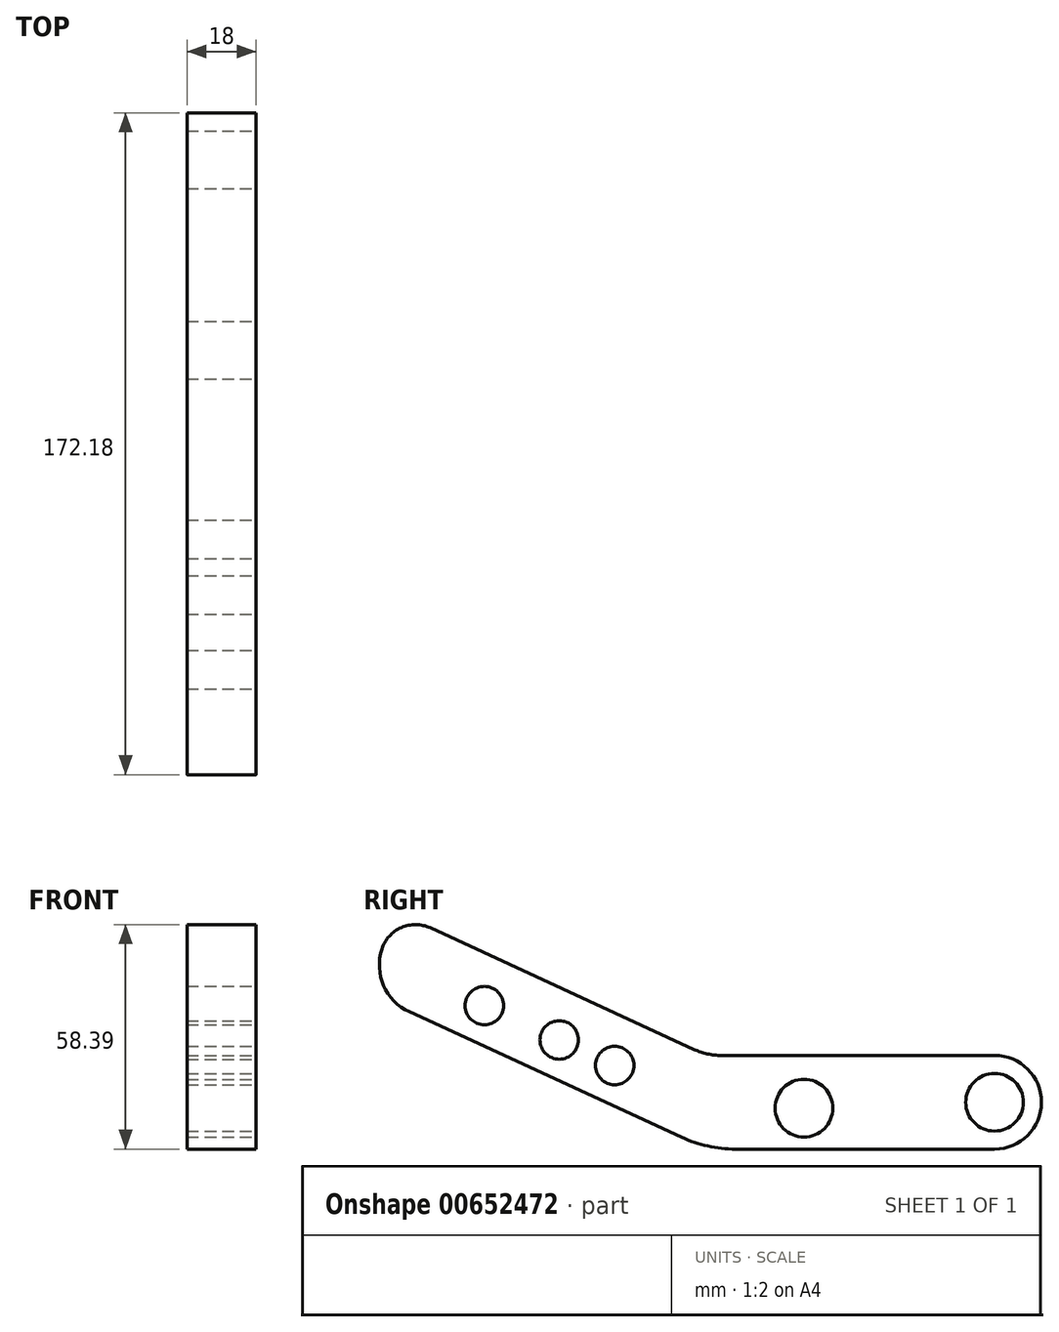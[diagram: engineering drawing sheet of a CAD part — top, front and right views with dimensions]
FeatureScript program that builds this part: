
annotation { "Feature Type Name" : "Feature", "Feature Type Description" : "" }
export const myFeature = defineFeature(function(context is Context, id is Id, definition is map)
    precondition{}
    {
        {
            var Q0;
            Q0=qCreatedBy(makeId("Right.planeOp"),FACE);
            var sketch = newSketch(context, id + "F0", { "sketchPlane" : qUnion([Q0])});
            skLineSegment(sketch, "E0", {"start": v(0, 13.71) * mm, "end": v(74.74, 13.71) * mm});
            skLineSegment(sketch, "E1", {"start": v(0, -10.64) * mm, "end": v(74.74, -10.64) * mm});
            skLineSegment(sketch, "E2", {"start": v(0, -10.64) * mm, "end": v(-77.46, 25.07) * mm});
            skLineSegment(sketch, "E3", {"start": v(0, 13.71) * mm, "end": v(-77.46, 49.43) * mm});
            skArc(sketch, "E4", {"start": v(74.74, -10.64) * mm, "mid": v(86.92, 1.53) * mm, "end": v(74.74, 13.71) * mm});
            skArc(sketch, "E5", {"start": v(-77.46, 49.43) * mm, "mid": v(-85.26, 37.25) * mm, "end": v(-77.46, 25.07) * mm});
            skLineSegment(sketch, "E6", {"start": v(0, 0) * mm, "end": v(-107.78, 49.69) * mm, "construction": true});
            skSolve(sketch);
        }
        {
            var Q0;
            Q0=makeQuery(id+"F0.imprint","IMPRINT",FACE,{"disambiguationData":[TD([[makeQuery(id+"F0.imprint","IMPRINT",EDGE,{"derivedFrom":sQuery(id+"F0.wireOp",EDGE,"E0")}),-1.0]])]});
            extrude(context, id + "F1", {"entities" : qUnion([Q0]), "oppositeDirection" : true, "depth" : 18 * mm, "offsetDistance" : 25 * mm});
        }
        {
            var Q0;
            Q0=makeQuery(id+"F1.opExtrude","SWEPT_EDGE",EDGE,{"disambiguationData":[OSD([sQuery(id+"F0.wireOp",EDGE,"E3"),sQuery(id+"F0.wireOp",EDGE,"E5")])]});
            fillet(context, id + "F2", {"entities" : qUnion([Q0]), "radius" : 9.2 * mm, "tangentPropagation" : true, "allowEdgeOverflow" : false});
        }
        {
            var Q0;
            Q0=makeQuery(id+"F0.imprint","IMPRINT",FACE,{"disambiguationData":[TD([[makeQuery(id+"F0.imprint","IMPRINT",EDGE,{"derivedFrom":sQuery(id+"F0.wireOp",EDGE,"E0")}),-1.0]])]});
            var sketch = newSketch(context, id + "F3", { "sketchPlane" : qUnion([Q0])});
            skCircle(sketch, "E7", {"center": v(-57.93, 26.67) * mm, "radius": 5.57 * mm});
            skCircle(sketch, "E8", {"center": v(-38.47, 17.74) * mm, "radius": 5.3 * mm});
            skCircle(sketch, "E9", {"center": v(-24.05, 11.1) * mm, "radius": 5.29 * mm});
            skCircle(sketch, "E10", {"center": v(75.08, 1.95) * mm, "radius": 7.96 * mm});
            skCircle(sketch, "E11", {"center": v(25.17, 0) * mm, "radius": 7.33 * mm});
            skSolve(sketch);
        }
        {
            var Q0;
            Q0=sQuery(id+"F3.wireOp",VERTEX,"E7.center");
            var Q1;
            Q1=sQuery(id+"F3.wireOp",VERTEX,"E8.center");
            var Q2;
            Q2=sQuery(id+"F3.wireOp",VERTEX,"E9.center");
            var Q3;
            Q3=makeQuery(id+"F1.opExtrude","SWEPT_BODY",BODY,{"disambiguationData":[OSD([sQuery(id+"F0.wireOp",EDGE,"E0"),sQuery(id+"F0.wireOp",EDGE,"E1"),sQuery(id+"F0.wireOp",EDGE,"E2"),sQuery(id+"F0.wireOp",EDGE,"E3"),sQuery(id+"F0.wireOp",EDGE,"E4"),sQuery(id+"F0.wireOp",EDGE,"E5")])]});
            hole(context, id + "F4", {"style" : HoleStyle.SIMPLE, "endStyle" : HoleEndStyle.THROUGH, "holeDiameter" : 10 * mm, "majorDiameter" : 5 * mm, "isTappedThrough" : true, "tappedDepth" : 12 * mm, "tapClearance" : 3, "locations" : qUnion([Q0, Q1, Q2]), "scope" : qUnion([Q3])});
        }
        {
            var Q0;
            Q0=makeQuery(id+"F1.opExtrude","SWEPT_EDGE",EDGE,{"disambiguationData":[OSD([sQuery(id+"F0.wireOp",EDGE,"E1"),sQuery(id+"F0.wireOp",EDGE,"E2")])]});
            fillet(context, id + "F5", {"entities" : qUnion([Q0]), "radius" : 33.5 * mm, "tangentPropagation" : true, "allowEdgeOverflow" : false});
        }
        {
            var Q0;
            Q0=makeQuery(id+"F1.opExtrude","SWEPT_EDGE",EDGE,{"disambiguationData":[OSD([sQuery(id+"F0.wireOp",EDGE,"E0"),sQuery(id+"F0.wireOp",EDGE,"E3")])]});
            fillet(context, id + "F6", {"entities" : qUnion([Q0]), "radius" : 17 * mm, "tangentPropagation" : true, "allowEdgeOverflow" : false});
        }
        {
            var Q0;
            Q0=sQuery(id+"F3.wireOp",VERTEX,"E11.center");
            var Q1;
            Q1=sQuery(id+"F0.wireOp",VERTEX,"E4.center");
            var Q2;
            Q2=makeQuery(id+"F1.opExtrude","SWEPT_BODY",BODY,{"disambiguationData":[OSD([sQuery(id+"F0.wireOp",EDGE,"E0"),sQuery(id+"F0.wireOp",EDGE,"E1"),sQuery(id+"F0.wireOp",EDGE,"E2"),sQuery(id+"F0.wireOp",EDGE,"E3"),sQuery(id+"F0.wireOp",EDGE,"E4"),sQuery(id+"F0.wireOp",EDGE,"E5")])]});
            hole(context, id + "F7", {"style" : HoleStyle.SIMPLE, "endStyle" : HoleEndStyle.THROUGH, "holeDiameter" : 15 * mm, "majorDiameter" : 5 * mm, "isTappedThrough" : true, "tappedDepth" : 12 * mm, "tapClearance" : 3, "locations" : qUnion([Q0, Q1]), "scope" : qUnion([Q2])});
        }
    });
